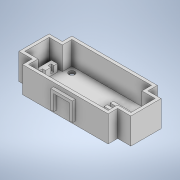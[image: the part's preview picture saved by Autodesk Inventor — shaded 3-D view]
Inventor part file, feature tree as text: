
AUTODESK INVENTOR PART (.ipt)
format: ipt  version: 2021 (Build 250183000, 183)  size: 259,072 bytes
history: native  units: mm
features: extrude x7, sketch x7, shell x3, plane x1, mirror x1
ambient origin geometry x8: Origin, YZ Plane, XZ Plane, XY Plane, X Axis, Y Axis, Z Axis, Center Point
bodies: Solid1 (feature_tree)
feature tree (19):
  extrude  "Extrusion1"  Depth=35.0mm
  extrude  "Extrusion2"  Depth=17.78mm
  shell  "Shell1"  Thickness=17.78mm
  extrude  "Extrusion3"  Depth=4.0mm
  shell  "Shell2"  Thickness=5.0mm
  extrude  "Extrusion4"  Depth=25.0mm
  plane  "Work Plane2"
  mirror  "Mirror1"
  extrude  "Extrusion5"  Depth=4.0mm TaperAngle=0.0deg
  shell  "Shell5"  Thickness=4.0mm
  extrude  "Extrusion6"  Depth=4.0mm TaperAngle=0.0deg
  extrude  "Extrusion12"  Depth=10.0mm
  sketch  "Sketch1"  dims[d0=150.4mm d1=35.0mm]
  sketch  "Sketch2"  dims[d4=33.1mm d5=0.0mm d6=17.78mm d7=17.78mm]
  sketch  "Sketch3"  dims[d8=12.8mm d9=0.0mm d10=4.0mm d11=5.0mm]
  sketch  "Sketch5"  dims[d12=43.77mm d13=25.0mm]
  sketch  "Sketch10"  dims[d14=29.3mm d15=4.0mm d16=0.0mm d17=4.0mm]
  sketch  "Sketch12"  dims[d18=21.3mm d19=4.0mm d20=0.0mm]
  sketch  "Sketch19"  dims[d26=-33.1mm d27=9.3mm d28=9.3mm d29=7.075mm d30=7.075mm d31=12.0mm d32=6.0mm d33=39.0mm d36=5.3mm d39=7.075mm d41=5.3mm d42=8.0mm d43=10.0mm d44=0.0mm d47=4.0mm d51=16.318829mm d54=7.5mm d55=0.0mm d60=15.097098mm d63=16.318829mm d64=4.0mm d65=4.0mm d66=4.0mm d67=4.0mm d68=24.6mm d69=4.5mm d70=4.5mm d126=8.0mm d127=4.0mm d128=4.0mm d129=8.0mm d130=4.0mm d131=4.0mm d132=8.0mm d133=4.0mm d134=4.0mm d135=8.0mm d136=4.0mm d137=4.0mm d138=10.0mm d139=0.0mm d109=0.5mm d110=0.872665mm d111=0.5mm d112=0.872665mm]
